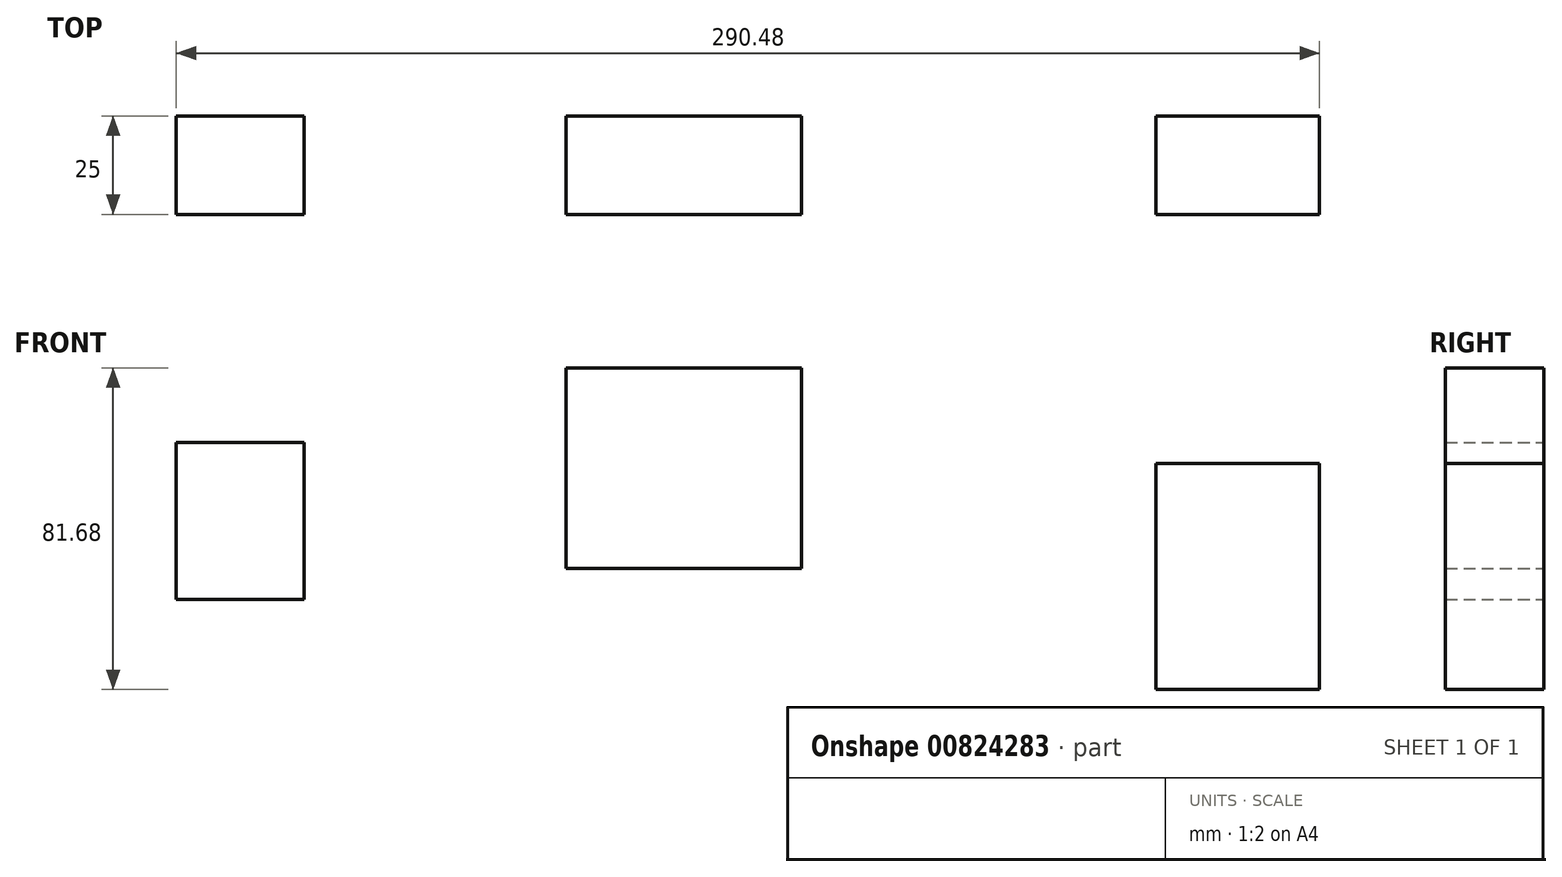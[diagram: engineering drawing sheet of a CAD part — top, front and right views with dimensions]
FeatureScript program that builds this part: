
annotation { "Feature Type Name" : "Feature", "Feature Type Description" : "" }
export const myFeature = defineFeature(function(context is Context, id is Id, definition is map)
    precondition{}
    {
        {
            var Q0;
            Q0=qCreatedBy(makeId("Front.planeOp"),FACE);
            var sketch = newSketch(context, id + "F0", { "sketchPlane" : qUnion([Q0])});
            skLineSegment(sketch, "E0.bottom", {"start": v(-132.26, 17.16) * mm, "end": v(-99.8, 17.16) * mm});
            skLineSegment(sketch, "E0.top", {"start": v(-132.26, 57.04) * mm, "end": v(-99.8, 57.04) * mm});
            skLineSegment(sketch, "E0.left", {"start": v(-132.26, 17.16) * mm, "end": v(-132.26, 57.04) * mm});
            skLineSegment(sketch, "E0.right", {"start": v(-99.8, 17.16) * mm, "end": v(-99.8, 57.04) * mm});
            skPoint(sketch, "E0.middle", {"position": v(-116.03, 37.1) * mm});
            skLineSegment(sketch, "E1.bottom", {"start": v(-33.27, 24.96) * mm, "end": v(26.6, 24.96) * mm});
            skLineSegment(sketch, "E1.top", {"start": v(-33.27, 75.93) * mm, "end": v(26.6, 75.93) * mm});
            skLineSegment(sketch, "E1.left", {"start": v(-33.27, 24.96) * mm, "end": v(-33.27, 75.93) * mm});
            skLineSegment(sketch, "E1.right", {"start": v(26.6, 24.96) * mm, "end": v(26.6, 75.93) * mm});
            skPoint(sketch, "E1.middle", {"position": v(-3.33, 50.44) * mm});
            skLineSegment(sketch, "E2.bottom", {"start": v(116.68, -5.75) * mm, "end": v(158.22, -5.75) * mm});
            skLineSegment(sketch, "E2.top", {"start": v(116.68, 51.68) * mm, "end": v(158.22, 51.68) * mm});
            skLineSegment(sketch, "E2.left", {"start": v(116.68, -5.75) * mm, "end": v(116.68, 51.68) * mm});
            skLineSegment(sketch, "E2.right", {"start": v(158.22, -5.75) * mm, "end": v(158.22, 51.68) * mm});
            skPoint(sketch, "E2.middle", {"position": v(137.45, 22.96) * mm});
            skSolve(sketch);
        }
        {
            var Q0;
            Q0 = qSketchRegion(id + "F0", true);
            extrude(context, id + "F1", {"entities" : qUnion([Q0]), "depth" : 25 * mm, "offsetDistance" : 25 * mm});
        }
    });
